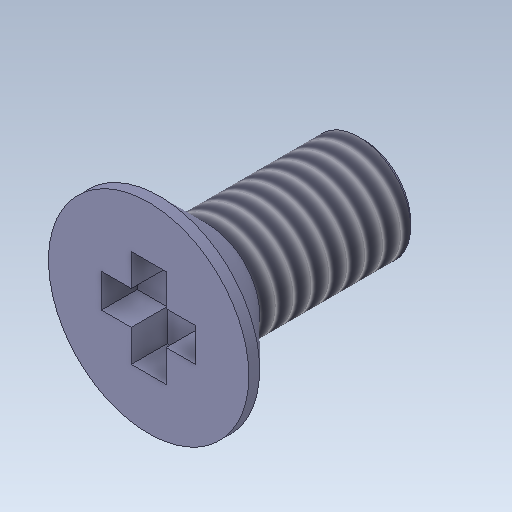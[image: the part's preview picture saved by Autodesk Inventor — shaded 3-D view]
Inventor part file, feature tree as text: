
AUTODESK INVENTOR PART (.ipt)
format: ipt  version: 2020 (Build 240168000, 168)  size: 162,304 bytes
history: native  units: mm
features: sketch x2, other x1, revolve x1, extrude x1, thread x1
ambient origin geometry x8: Origin, YZ Plane, XZ Plane, XY Plane, X Axis, Y Axis, Z Axis, Center Point
bodies: Body1 (feature_tree)
feature tree (6):
  other  "Твердое тело1"
  revolve  "Вращение1"
  extrude  "Выдавливание1"  TaperAngle=90.0deg  [1 undecoded]
  thread  "Резьба1"
  sketch  "Эскиз1"
  sketch  "Эскиз2"
note: 1 required parameter value undecoded (feature->parameter linkage not recoverable at this tier; creation-order binding heuristic only, values carry confidence <= 0.55)
